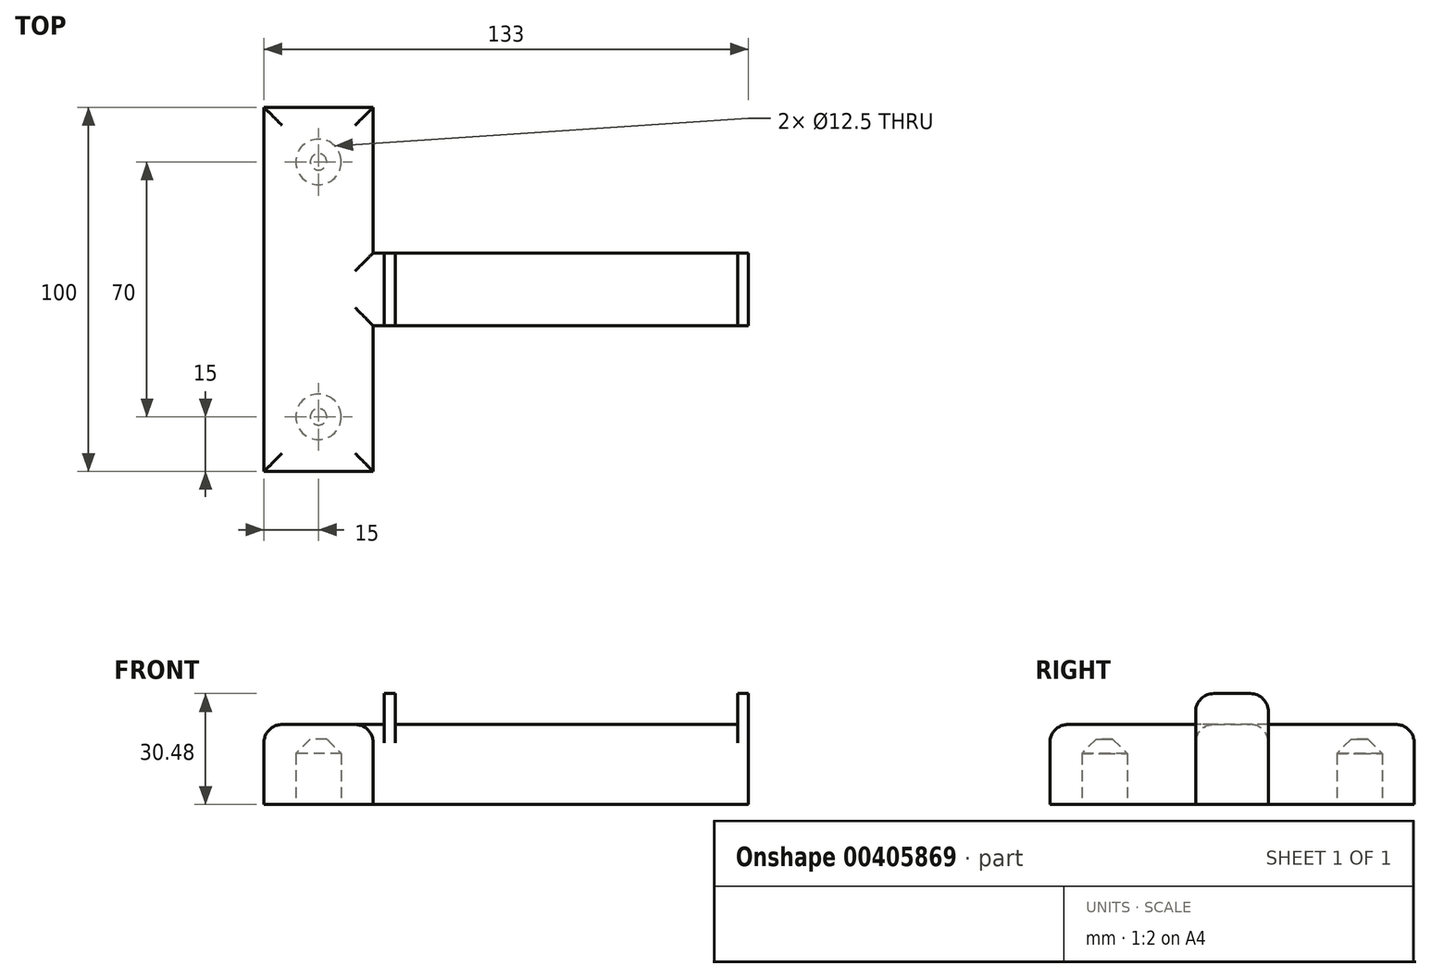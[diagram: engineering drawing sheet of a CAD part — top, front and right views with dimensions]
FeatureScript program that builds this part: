
annotation { "Feature Type Name" : "Feature", "Feature Type Description" : "" }
export const myFeature = defineFeature(function(context is Context, id is Id, definition is map)
    precondition{}
    {
        {
            var Q0;
            Q0=qCreatedBy(makeId("Top.planeOp"),FACE);
            var sketch = newSketch(context, id + "F0", { "sketchPlane" : qUnion([Q0])});
            skCircle(sketch, "E0", {"center": v(0, -35) * mm, "radius": 6.25 * mm});
            skCircle(sketch, "E1", {"center": v(0, 35) * mm, "radius": 6.25 * mm});
            skLineSegment(sketch, "E2.rect.bottom", {"start": v(15, 50) * mm, "end": v(-15, 50) * mm});
            skLineSegment(sketch, "E2.rect.top", {"start": v(15, -50) * mm, "end": v(-15, -50) * mm});
            skLineSegment(sketch, "E2.rect.left", {"start": v(15, 50) * mm, "end": v(15, -50) * mm});
            skLineSegment(sketch, "E2.rect.right", {"start": v(-15, 50) * mm, "end": v(-15, -50) * mm});
            skPoint(sketch, "E2.rect.middle", {"position": v(0, 0) * mm});
            skLineSegment(sketch, "E3.bottom", {"start": v(0, -10) * mm, "end": v(115, -10) * mm});
            skLineSegment(sketch, "E3.top", {"start": v(0, 10) * mm, "end": v(115, 10) * mm});
            skLineSegment(sketch, "E3.left", {"start": v(0, -10) * mm, "end": v(0, 10) * mm});
            skLineSegment(sketch, "E3.right", {"start": v(115, -10) * mm, "end": v(115, 10) * mm});
            skLineSegment(sketch, "E4", {"start": v(115, -10) * mm, "end": v(118, -10) * mm});
            skLineSegment(sketch, "E5", {"start": v(118, -10) * mm, "end": v(118, 10) * mm});
            skLineSegment(sketch, "E6", {"start": v(118, 10) * mm, "end": v(115, 10) * mm});
            skLineSegment(sketch, "E7", {"start": v(21.02, 10) * mm, "end": v(21.02, -10) * mm});
            skLineSegment(sketch, "E8", {"start": v(18.02, 10) * mm, "end": v(18.02, -10) * mm});
            skSolve(sketch);
        }
        {
            var Q0;
            Q0=makeQuery(id+"F0.imprint","IMPRINT",FACE,{"disambiguationData":[TD([[makeQuery(id+"F0.imprint","IMPRINT",EDGE,{"derivedFrom":sQuery(id+"F0.wireOp",EDGE,"E0")}),-1.0]])]});
            var Q1;
            {var subQ0=sQuery(id+"F0.wireOp",EDGE,"E3.left");Q1=makeQuery(id+"F0.imprint","IMPRINT",FACE,{"disambiguationData":[TD([[makeQuery(id+"F0.imprint","IMPRINT",EDGE,{"derivedFrom":subQ0}),-1.0]])]});}
            var Q2;
            {var subQ0=sQuery(id+"F0.wireOp",EDGE,"E3.right");Q2=makeQuery(id+"F0.imprint","IMPRINT",FACE,{"disambiguationData":[TD([[makeQuery(id+"F0.imprint","IMPRINT",EDGE,{"derivedFrom":subQ0}),1.0]])]});}
            var Q3;
            Q3=makeQuery(id+"F0.imprint","IMPRINT",FACE,{"disambiguationData":[TD([[makeQuery(id+"F0.imprint","IMPRINT",EDGE,{"derivedFrom":sQuery(id+"F0.wireOp",EDGE,"E0")}),1.0]])]});
            var Q4;
            Q4=makeQuery(id+"F0.imprint","IMPRINT",FACE,{"disambiguationData":[TD([[makeQuery(id+"F0.imprint","IMPRINT",EDGE,{"derivedFrom":sQuery(id+"F0.wireOp",EDGE,"E1")}),1.0]])]});
            var Q5;
            {var subQ3=sQuery(id+"F0.wireOp",EDGE,"E8");Q5=makeQuery(id+"F0.imprint","IMPRINT",FACE,{"disambiguationData":[TD([[makeQuery(id+"F0.imprint","IMPRINT",EDGE,{"derivedFrom":subQ3}),-1.0]])]});}
            var Q6;
            {var subQ1=sQuery(id+"F0.wireOp",EDGE,"E7");Q6=makeQuery(id+"F0.imprint","IMPRINT",FACE,{"disambiguationData":[TD([[makeQuery(id+"F0.imprint","IMPRINT",EDGE,{"derivedFrom":subQ1}),-1.0]])]});}
            extrude(context, id + "F1", {"entities" : qUnion([Q0, Q1, Q2, Q3, Q4, Q5, Q6]), "depth" : 22 * mm});
        }
        {
            var Q0;
            Q0=makeQuery(id+"F0.imprint","IMPRINT",FACE,{"disambiguationData":[TD([[makeQuery(id+"F0.imprint","IMPRINT",EDGE,{"derivedFrom":sQuery(id+"F0.wireOp",EDGE,"E3.right")}),-1.0]])]});
            var Q1;
            {var subQ1=sQuery(id+"F0.wireOp",EDGE,"E7");Q1=makeQuery(id+"F0.imprint","IMPRINT",FACE,{"disambiguationData":[TD([[makeQuery(id+"F0.imprint","IMPRINT",EDGE,{"derivedFrom":subQ1}),-1.0]])]});}
            extrude(context, id + "F2", {"entities" : qUnion([Q0, Q1]), "operationType" : NewBodyOperationType.ADD, "depth" : 30.48 * mm});
        }
        {
            var Q0;
            Q0=makeQuery(id+"F0.imprint","IMPRINT",FACE,{"disambiguationData":[TD([[makeQuery(id+"F0.imprint","IMPRINT",EDGE,{"derivedFrom":sQuery(id+"F0.wireOp",EDGE,"E0")}),1.0]])]});
            var Q1;
            Q1=makeQuery(id+"F0.imprint","IMPRINT",FACE,{"disambiguationData":[TD([[makeQuery(id+"F0.imprint","IMPRINT",EDGE,{"derivedFrom":sQuery(id+"F0.wireOp",EDGE,"E1")}),1.0]])]});
            extrude(context, id + "F3", {"entities" : qUnion([Q0, Q1]), "operationType" : NewBodyOperationType.REMOVE, "depth" : 18 * mm});
        }
        {
            var Q0;
            Q0=makeQuery(id+"F3.boolean.opBoolean","COPY",EDGE,{"derivedFrom":makeQuery(id+"F3.opExtrude","CAP_EDGE",EDGE,{"disambiguationData":[OSD([sQuery(id+"F0.wireOp",EDGE,"E0")])],"isStart":false})});
            var Q1;
            Q1=makeQuery(id+"F3.boolean.opBoolean","COPY",EDGE,{"derivedFrom":makeQuery(id+"F3.opExtrude","CAP_EDGE",EDGE,{"disambiguationData":[OSD([sQuery(id+"F0.wireOp",EDGE,"E1")])],"isStart":false})});
            chamfer(context, id + "F4", {"entities" : qUnion([Q0, Q1]), "width" : 4 * mm, "tangentPropagation" : true});
        }
        {
            var Q0;
            Q0=makeQuery(id+"F1.opExtrude","CAP_EDGE",EDGE,{"disambiguationData":[OSD([sQuery(id+"F0.wireOp",EDGE,"E3.bottom")])],"isStart":false});
            var Q1;
            Q1=makeQuery(id+"F1.opExtrude","CAP_EDGE",EDGE,{"disambiguationData":[OSD([sQuery(id+"F0.wireOp",EDGE,"E3.top")])],"isStart":false});
            var Q2;
            Q2=makeQuery(id+"F2.opExtrude","CAP_EDGE",EDGE,{"disambiguationData":[OSD([sQuery(id+"F0.wireOp",EDGE,"E4")])],"isStart":false});
            var Q3;
            Q3=makeQuery(id+"F2.opExtrude","CAP_EDGE",EDGE,{"disambiguationData":[OSD([sQuery(id+"F0.wireOp",EDGE,"E6")])],"isStart":false});
            var Q4;
            {var subQ0=sQuery(id+"F0.wireOp",EDGE,"E2.rect.left");Q4=makeQuery(id+"F1.opExtrude","CAP_EDGE",EDGE,{"disambiguationData":[OSD([subQ0]),TDD([makeQuery(id+"F0.imprint","IMPRINT",EDGE,{"disambiguationData":[TD([[makeQuery(id+"F0.imprint","INTERSECT",VERTEX,{"derivedFrom":[sQuery(id+"F0.wireOp",EDGE,"E2.rect.top"),subQ0]}),1.0]])],"derivedFrom":subQ0})])],"isStart":false});}
            var Q5;
            {var subQ0=sQuery(id+"F0.wireOp",EDGE,"E2.rect.left");Q5=makeQuery(id+"F1.opExtrude","CAP_EDGE",EDGE,{"disambiguationData":[OSD([subQ0]),TDD([makeQuery(id+"F0.imprint","IMPRINT",EDGE,{"disambiguationData":[TD([[makeQuery(id+"F0.imprint","INTERSECT",VERTEX,{"derivedFrom":[sQuery(id+"F0.wireOp",EDGE,"E2.rect.bottom"),subQ0]}),-1.0]])],"derivedFrom":subQ0})])],"isStart":false});}
            var Q6;
            Q6=makeQuery(id+"F1.opExtrude","CAP_EDGE",EDGE,{"disambiguationData":[OSD([sQuery(id+"F0.wireOp",EDGE,"E2.rect.right")])],"isStart":false});
            var Q7;
            Q7=makeQuery(id+"F1.opExtrude","CAP_EDGE",EDGE,{"disambiguationData":[OSD([sQuery(id+"F0.wireOp",EDGE,"E2.rect.top")])],"isStart":false});
            var Q8;
            Q8=makeQuery(id+"F1.opExtrude","CAP_EDGE",EDGE,{"disambiguationData":[OSD([sQuery(id+"F0.wireOp",EDGE,"E2.rect.bottom")])],"isStart":false});
            var Q9;
            Q9=makeQuery(id+"F2.opExtrude","CAP_EDGE",EDGE,{"disambiguationData":[OSD([sQuery(id+"F0.wireOp",EDGE,"E3.bottom")])],"isStart":false});
            var Q10;
            Q10=makeQuery(id+"F2.opExtrude","CAP_EDGE",EDGE,{"disambiguationData":[OSD([sQuery(id+"F0.wireOp",EDGE,"E3.top")])],"isStart":false});
            fillet(context, id + "F5", {"entities" : qUnion([Q0, Q1, Q2, Q3, Q4, Q5, Q6, Q7, Q8, Q9, Q10]), "radius" : 5 * mm, "tangentPropagation" : true, "allowEdgeOverflow" : false});
        }
    });
